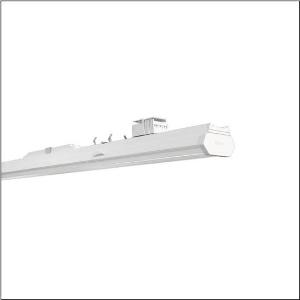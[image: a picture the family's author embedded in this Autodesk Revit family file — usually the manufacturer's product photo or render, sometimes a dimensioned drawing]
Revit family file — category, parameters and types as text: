
# Revit family: licross_21_protected_mo_52td11mn4a5g
name_source: partatom
category: Lighting Fixtures
units: mm (PartAtom-declared; Revit-internal decimal feet)

## family parameters
Cut with Voids When Loaded = No
Host = Face
Light Source = No
Part Type = Normal
Room Calculation Point = No
Round Connector Dimension = Use Diameter
Shared = No

## types (1)
- --- (1 x LED, 10700 lm, 60.5 W, 4000K)
    Apparent Load = 61 VA
    CIE Flux Codes = 83 94 98 100 100
    Color Rendering = 80
    Color Temperature = 4000K
    Default Elevation = 1800 mm
    Description = Licross 21 Protected MO, luminaire insert, of sheet steel, galvanised, coil coated, white, length: 1.500mm, width: 66mm, height: 67mm, LED rated luminous flux: 10.700lm, light colour: 840, SDCM (Standard Deviation of Colour Matching)MacAdam ≤ 3 SDCM (initial), control gear: ON/OFF Multilumen, with plug, 3-pole, with phase selection, mains connection: 220..240V, AC, 50/60Hz, rated input power: 61W, internal wiring halogen-free, primary light control with lens, of plastic, primary optical cover: cover, of PMMA, light emission: direct distribution, primary light characteristic: symmetric, protection rating (complete): IP54, insulation class (complete): insulation class I (protective earthing), certification: CE, ENEC, VDE, UKCA, protection symbol: D if used in an environment with non-conductive dust loads with corresponding accessories, impact resistance: IK06, permissible ambient temperature for indoor applications: -35..+45°C, corresponds to IFS (International Featured Standards) requirements for safety and quality in the food industry, reducing of maximum allowable ambient temperature of 5°C with ceiling mounting, LABS conformity tested according to VDMA 24364:2018-05, The light source and the operating device comply with the requirements of the Ecodesign Regulation (EU) 2019/2020 and are replaceable in accordance with this regulation, packaging unit: 1 piece
    Height = 92 mm
    Lamp = 1 x LED
    Lamp Light Flux = 10700 lm
    Lamp Power = 60.5 W
    Lamp count = 1
    Length = 1500 mm
    Luminous efficacy = 177 lm/W
    Manufacturer = Siteco
    ModVariant = No
    Model = 52TD11MN4A5G
    Mounting Place = Ceiling
    Mounting Type = Pendant
    Number of Poles = 1
    OnlyDefault = Yes
    Power Factor = 1
    Product Name = Licross 21 Protected MO
    Product group = luminaire insert | ceiling pendant
    ProductGroupID = 901
    Protection Class = Protection class I
    Protection Degree = IP 54
    RLX_Detail_Level = 1
    RLX_Emergency_Light_Flux = 0 lm
    RLX_Emergency_Type = 0
    RLX_Emergency_Type_DB = No
    RlxData = <blob elided: 22093 chars, md5=442e021f>
    Socket = socket
    Standby Power = 0 W
    System Light Flux = 10700 lm
    System Power = 61 W
    Type Comments = factory setting: luminous flux: 100 % | (A | C | E) | 140 mA
    Type Image = l_1256148.jpg
    URL = http://relux.com
    VarID = @adj_110579
    Voltage = 0 V
    Weight = 0.00 kg
    Width = 88 mm

## geometry (parser evidence)
native form markers: Blend x4, Sweep x11
no freeform markers — native parametric forms only
